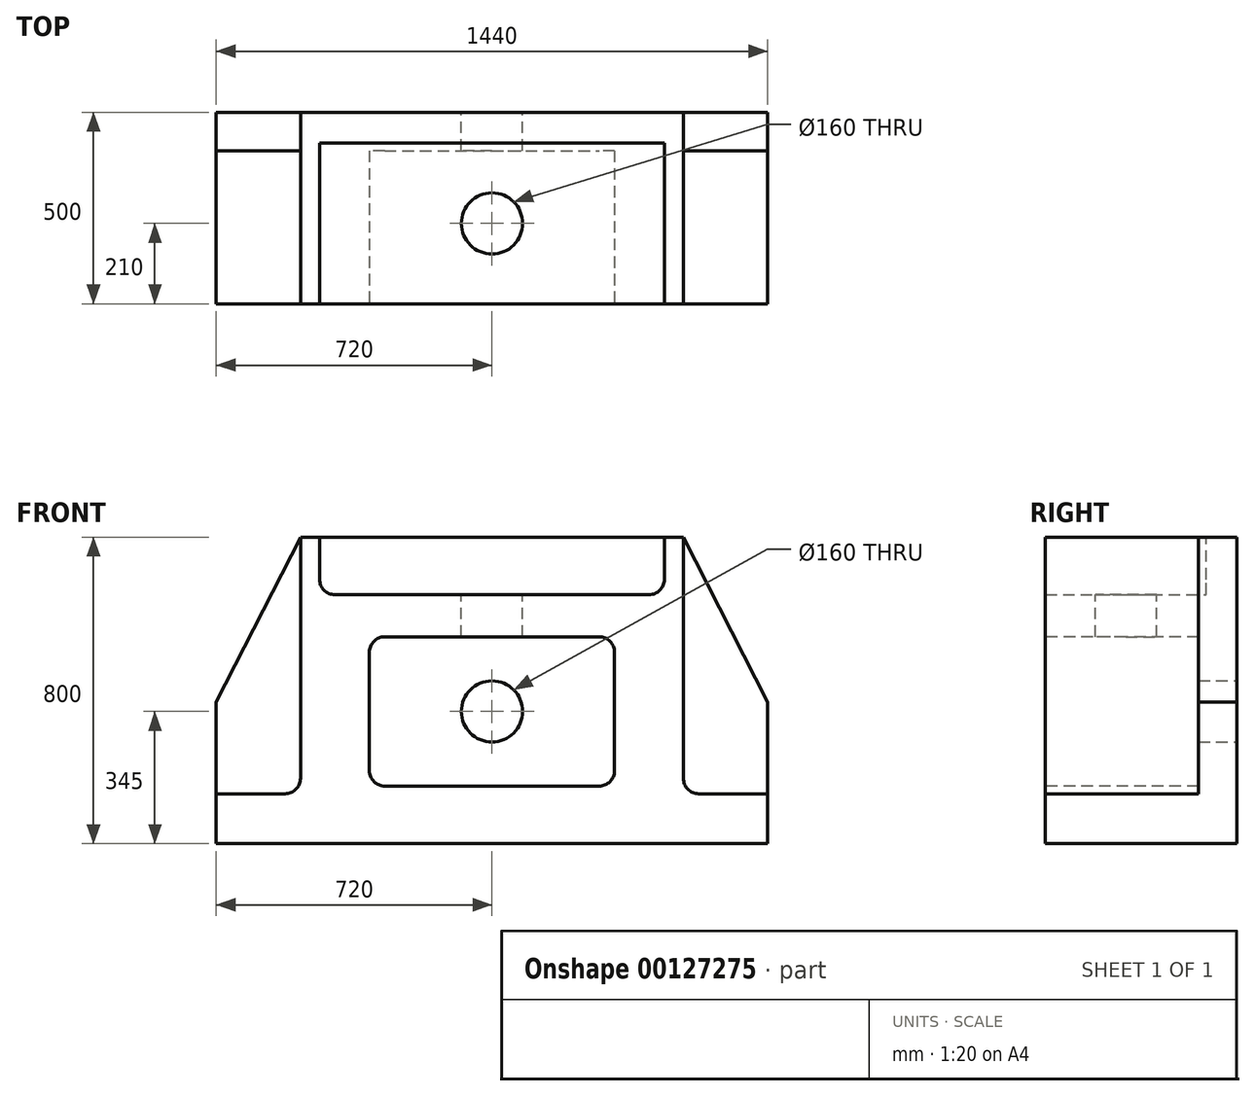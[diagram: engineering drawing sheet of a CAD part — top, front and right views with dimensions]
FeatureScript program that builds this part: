
annotation { "Feature Type Name" : "Feature", "Feature Type Description" : "" }
export const myFeature = defineFeature(function(context is Context, id is Id, definition is map)
    precondition{}
    {
        {
            var Q0;
            Q0=qCreatedBy(makeId("Front.planeOp"),FACE);
            var sketch = newSketch(context, id + "F0", { "sketchPlane" : qUnion([Q0])});
            skLineSegment(sketch, "E0.bottom", {"start": v(720, 400) * mm, "end": v(-720, 400) * mm});
            skLineSegment(sketch, "E0.top", {"start": v(720, -400) * mm, "end": v(-720, -400) * mm});
            skLineSegment(sketch, "E0.left", {"start": v(720, 400) * mm, "end": v(720, -400) * mm});
            skLineSegment(sketch, "E0.right", {"start": v(-720, 400) * mm, "end": v(-720, -400) * mm});
            skPoint(sketch, "E0.middle", {"position": v(0, 0) * mm});
            skSolve(sketch);
        }
        {
            var Q0;
            Q0 = qSketchRegion(id + "F0", true);
            extrude(context, id + "F1", {"entities" : qUnion([Q0]), "depth" : 500 * mm});
        }
        {
            var Q0;
            Q0=makeQuery(id+"F1.opExtrude","CAP_FACE",FACE,{"disambiguationData":[OSD([sQuery(id+"F0.wireOp",EDGE,"E0.bottom"),sQuery(id+"F0.wireOp",EDGE,"E0.top"),sQuery(id+"F0.wireOp",EDGE,"E0.left"),sQuery(id+"F0.wireOp",EDGE,"E0.right")])],"isStart":false});
            var sketch = newSketch(context, id + "F2", { "sketchPlane" : qUnion([Q0])});
            skLineSegment(sketch, "E1.bottom", {"start": v(-280, 140) * mm, "end": v(280, 140) * mm});
            skLineSegment(sketch, "E1.top", {"start": v(-280, -250) * mm, "end": v(280, -250) * mm});
            skLineSegment(sketch, "E1.left", {"start": v(-320, 100) * mm, "end": v(-320, -210) * mm});
            skLineSegment(sketch, "E1.right", {"start": v(320, 100) * mm, "end": v(320, -210) * mm});
            skPoint(sketch, "E2.visualSharp", {"position": v(-320, 140) * mm});
            skArc(sketch, "E2.filletArc", {"start": v(-280, 140) * mm, "mid": v(-308.28, 128.28) * mm, "end": v(-320, 100) * mm});
            skPoint(sketch, "E3.visualSharp", {"position": v(320, 140) * mm});
            skArc(sketch, "E3.filletArc", {"start": v(320, 100) * mm, "mid": v(308.28, 128.28) * mm, "end": v(280, 140) * mm});
            skPoint(sketch, "E4.visualSharp", {"position": v(320, -250) * mm});
            skArc(sketch, "E4.filletArc", {"start": v(280, -250) * mm, "mid": v(308.28, -238.28) * mm, "end": v(320, -210) * mm});
            skPoint(sketch, "E5.visualSharp", {"position": v(-320, -250) * mm});
            skArc(sketch, "E5.filletArc", {"start": v(-320, -210) * mm, "mid": v(-308.28, -238.28) * mm, "end": v(-280, -250) * mm});
            skSolve(sketch);
        }
        {
            var Q0;
            Q0 = qSketchRegion(id + "F2", true);
            extrude(context, id + "F3", {"entities" : qUnion([Q0]), "operationType" : NewBodyOperationType.REMOVE, "oppositeDirection" : true, "depth" : 400 * mm});
        }
        {
            var Q0;
            Q0=makeQuery(id+"F1.opExtrude","CAP_FACE",FACE,{"disambiguationData":[OSD([sQuery(id+"F0.wireOp",EDGE,"E0.bottom"),sQuery(id+"F0.wireOp",EDGE,"E0.top"),sQuery(id+"F0.wireOp",EDGE,"E0.left"),sQuery(id+"F0.wireOp",EDGE,"E0.right")])],"isStart":false});
            var sketch = newSketch(context, id + "F4", { "sketchPlane" : qUnion([Q0])});
            skLineSegment(sketch, "E6", {"start": v(-720, -270) * mm, "end": v(-540, -270) * mm});
            skLineSegment(sketch, "E7", {"start": v(-500, -230) * mm, "end": v(-500, 400) * mm});
            skLineSegment(sketch, "E8", {"start": v(720, -270) * mm, "end": v(540, -270) * mm});
            skLineSegment(sketch, "E9", {"start": v(500, -230) * mm, "end": v(500, 400) * mm});
            skPoint(sketch, "E10.visualSharp", {"position": v(-500, -270) * mm});
            skArc(sketch, "E10.filletArc", {"start": v(-540, -270) * mm, "mid": v(-511.72, -258.28) * mm, "end": v(-500, -230) * mm});
            skPoint(sketch, "E11.visualSharp", {"position": v(500, -270) * mm});
            skArc(sketch, "E11.filletArc", {"start": v(500, -230) * mm, "mid": v(511.72, -258.28) * mm, "end": v(540, -270) * mm});
            skSolve(sketch);
        }
        {
            var Q0;
            Q0 = qSketchRegion(id + "F4", true);
            var Q1;
            {var subQ4=sQuery(id+"F4.wireOp",EDGE,"E6");Q1=makeQuery(id+"F4.imprint","IMPRINT",FACE,{"disambiguationData":[TD([[makeQuery(id+"F4.imprint","IMPRINT",EDGE,{"derivedFrom":subQ4}),1.0]])]});}
            var Q2;
            {var subQ4=sQuery(id+"F4.wireOp",EDGE,"E8");Q2=makeQuery(id+"F4.imprint","IMPRINT",FACE,{"disambiguationData":[TD([[makeQuery(id+"F4.imprint","IMPRINT",EDGE,{"derivedFrom":subQ4}),-1.0]])]});}
            extrude(context, id + "F5", {"entities" : qUnion([Q0, Q1, Q2]), "operationType" : NewBodyOperationType.REMOVE, "oppositeDirection" : true, "depth" : 400 * mm});
        }
        {
            var Q0;
            Q0=makeQuery(id+"F5.boolean.opBoolean","COPY",FACE,{"derivedFrom":makeQuery(id+"F5.opExtrude","CAP_FACE",FACE,{"disambiguationData":[OSD([sQuery(id+"F0.wireOp",EDGE,"E0.bottom"),sQuery(id+"F0.wireOp",EDGE,"E0.left"),sQuery(id+"F4.wireOp",EDGE,"E8"),sQuery(id+"F4.wireOp",EDGE,"E9"),sQuery(id+"F4.wireOp",EDGE,"E11.filletArc")])],"isStart":false})});
            var sketch = newSketch(context, id + "F6", { "sketchPlane" : qUnion([Q0])});
            skLineSegment(sketch, "E12", {"start": v(720, -270) * mm, "end": v(720, -30) * mm});
            skLineSegment(sketch, "E13", {"start": v(720, -30) * mm, "end": v(500, 400) * mm});
            skSolve(sketch);
        }
        {
            var Q0;
            Q0 = qSketchRegion(id + "F6", true);
            var Q1;
            {var subQ0=sQuery(id+"F6.wireOp",EDGE,"E13");Q1=makeQuery(id+"F6.imprint","IMPRINT",FACE,{"disambiguationData":[TD([[makeQuery(id+"F6.imprint","IMPRINT",EDGE,{"derivedFrom":subQ0}),-1.0]])]});}
            extrude(context, id + "F7", {"entities" : qUnion([Q0, Q1]), "operationType" : NewBodyOperationType.REMOVE, "endBound" : BoundingType.THROUGH_ALL, "oppositeDirection" : true, "depth" : 25.4 * mm});
        }
        {
            var Q0;
            Q0=makeQuery(id+"F5.boolean.opBoolean","COPY",FACE,{"derivedFrom":makeQuery(id+"F5.opExtrude","CAP_FACE",FACE,{"disambiguationData":[OSD([sQuery(id+"F0.wireOp",EDGE,"E0.bottom"),sQuery(id+"F0.wireOp",EDGE,"E0.right"),sQuery(id+"F4.wireOp",EDGE,"E6"),sQuery(id+"F4.wireOp",EDGE,"E7"),sQuery(id+"F4.wireOp",EDGE,"E10.filletArc")])],"isStart":false})});
            var sketch = newSketch(context, id + "F8", { "sketchPlane" : qUnion([Q0])});
            skLineSegment(sketch, "E14", {"start": v(-720, -270) * mm, "end": v(-720, -30) * mm});
            skLineSegment(sketch, "E15", {"start": v(-720, -30) * mm, "end": v(-500, 400) * mm});
            skSolve(sketch);
        }
        {
            var Q0;
            {var subQ0=sQuery(id+"F8.wireOp",EDGE,"E15");Q0=makeQuery(id+"F8.imprint","IMPRINT",FACE,{"disambiguationData":[TD([[makeQuery(id+"F8.imprint","IMPRINT",EDGE,{"derivedFrom":subQ0}),1.0]])]});}
            extrude(context, id + "F9", {"entities" : qUnion([Q0]), "operationType" : NewBodyOperationType.REMOVE, "endBound" : BoundingType.THROUGH_ALL, "oppositeDirection" : true, "depth" : 25.4 * mm});
        }
        {
            var Q0;
            Q0=makeQuery(id+"F1.opExtrude","SWEPT_FACE",FACE,{"disambiguationData":[OSD([sQuery(id+"F0.wireOp",EDGE,"E0.bottom")])]});
            var sketch = newSketch(context, id + "F10", { "sketchPlane" : qUnion([Q0])});
            skLineSegment(sketch, "E16.bottom", {"start": v(-450, -500) * mm, "end": v(450, -500) * mm});
            skLineSegment(sketch, "E16.top", {"start": v(-450, -80) * mm, "end": v(450, -80) * mm});
            skLineSegment(sketch, "E16.left", {"start": v(-450, -500) * mm, "end": v(-450, -80) * mm});
            skLineSegment(sketch, "E16.right", {"start": v(450, -500) * mm, "end": v(450, -80) * mm});
            skSolve(sketch);
        }
        {
            var Q0;
            Q0 = qSketchRegion(id + "F10", true);
            extrude(context, id + "F11", {"entities" : qUnion([Q0]), "operationType" : NewBodyOperationType.REMOVE, "oppositeDirection" : true, "depth" : 150 * mm});
        }
        {
            var Q0;
            Q0=makeQuery(id+"F11.boolean.opBoolean","COPY",EDGE,{"derivedFrom":makeQuery(id+"F11.opExtrude","CAP_EDGE",EDGE,{"disambiguationData":[OSD([sQuery(id+"F10.wireOp",EDGE,"E16.left")])],"isStart":false})});
            var Q1;
            Q1=makeQuery(id+"F11.boolean.opBoolean","COPY",EDGE,{"derivedFrom":makeQuery(id+"F11.opExtrude","CAP_EDGE",EDGE,{"disambiguationData":[OSD([sQuery(id+"F10.wireOp",EDGE,"E16.right")])],"isStart":false})});
            fillet(context, id + "F12", {"entities" : qUnion([Q0, Q1]), "radius" : 40 * mm, "tangentPropagation" : true, "allowEdgeOverflow" : false});
        }
        {
            var Q0;
            Q0=makeQuery(id+"F11.boolean.opBoolean","COPY",FACE,{"derivedFrom":makeQuery(id+"F11.opExtrude","CAP_FACE",FACE,{"disambiguationData":[OSD([sQuery(id+"F10.wireOp",EDGE,"E16.bottom"),sQuery(id+"F10.wireOp",EDGE,"E16.top"),sQuery(id+"F10.wireOp",EDGE,"E16.left"),sQuery(id+"F10.wireOp",EDGE,"E16.right")])],"isStart":false})});
            var sketch = newSketch(context, id + "F13", { "sketchPlane" : qUnion([Q0])});
            skCircle(sketch, "E17", {"center": v(0, -290) * mm, "radius": 80 * mm});
            skPoint(sketch, "E17.centerSnap0", {"position": v(410, -290) * mm});
            skSolve(sketch);
        }
        {
            var Q0;
            Q0 = qSketchRegion(id + "F13", true);
            extrude(context, id + "F14", {"entities" : qUnion([Q0]), "operationType" : NewBodyOperationType.REMOVE, "oppositeDirection" : true, "depth" : 150 * mm});
        }
        {
            var Q0;
            Q0=makeQuery(id+"F1.opExtrude","CAP_FACE",FACE,{"disambiguationData":[OSD([sQuery(id+"F0.wireOp",EDGE,"E0.bottom"),sQuery(id+"F0.wireOp",EDGE,"E0.top"),sQuery(id+"F0.wireOp",EDGE,"E0.left"),sQuery(id+"F0.wireOp",EDGE,"E0.right")])],"isStart":true});
            var sketch = newSketch(context, id + "F15", { "sketchPlane" : qUnion([Q0])});
            skPoint(sketch, "E18.endSnap0", {"position": v(0, -400) * mm});
            skCircle(sketch, "E19", {"center": v(0, -55) * mm, "radius": 80 * mm});
            skSolve(sketch);
        }
        {
            var Q0;
            Q0 = qSketchRegion(id + "F15", true);
            extrude(context, id + "F16", {"entities" : qUnion([Q0]), "operationType" : NewBodyOperationType.REMOVE, "endBound" : BoundingType.THROUGH_ALL, "oppositeDirection" : true, "depth" : 25.4 * mm});
        }
    });
